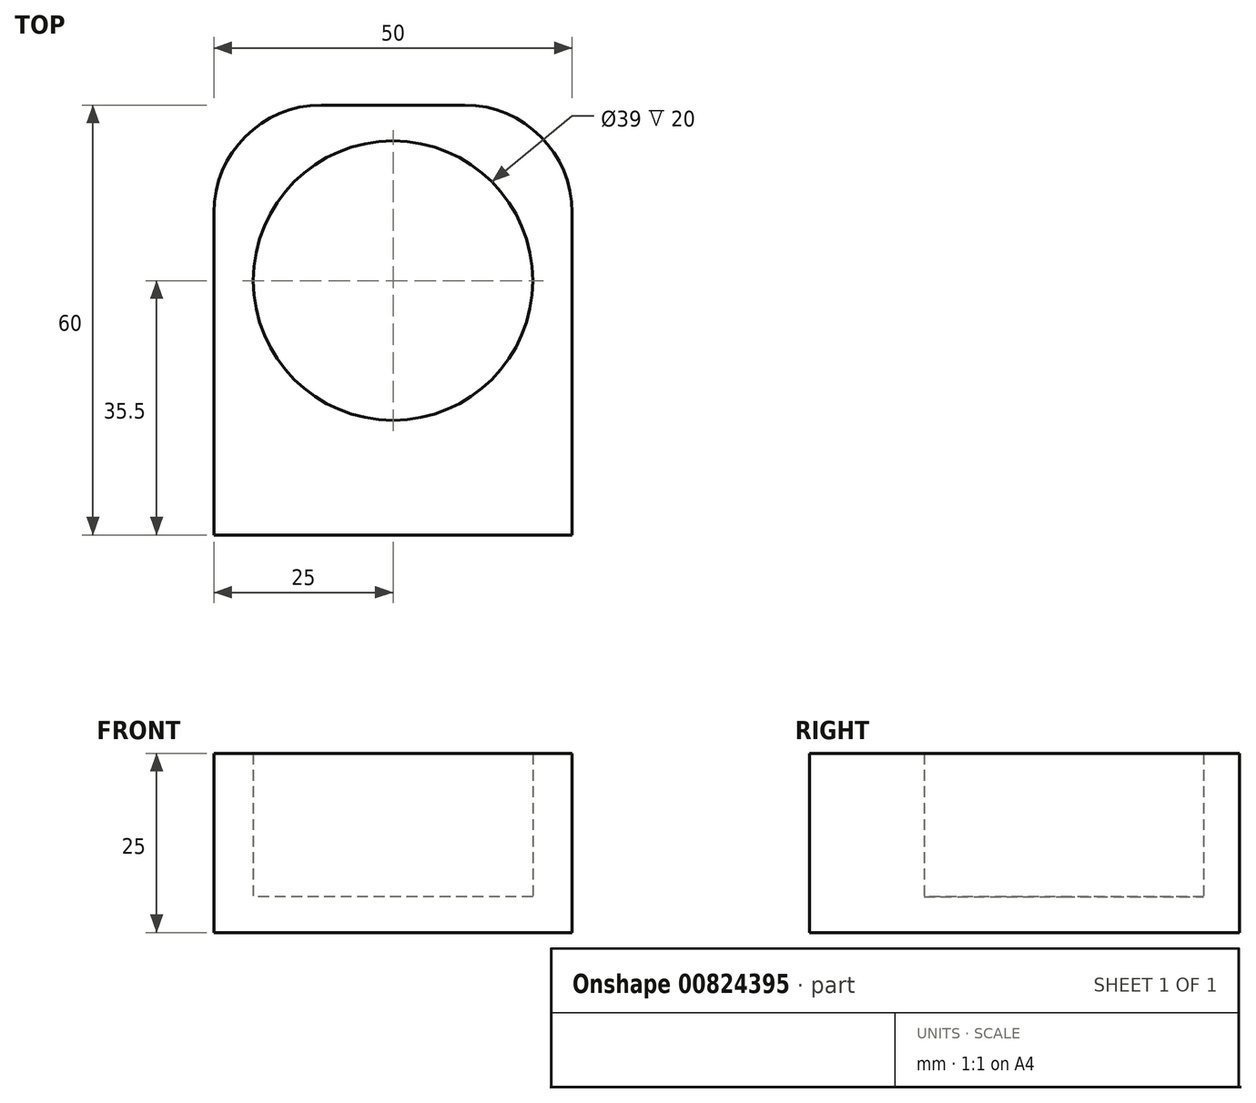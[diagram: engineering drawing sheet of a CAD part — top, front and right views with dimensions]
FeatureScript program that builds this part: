
annotation { "Feature Type Name" : "Feature", "Feature Type Description" : "" }
export const myFeature = defineFeature(function(context is Context, id is Id, definition is map)
    precondition{}
    {
        {
            var Q0;
            Q0=qCreatedBy(makeId("Top.planeOp"),FACE);
            var sketch = newSketch(context, id + "F0", { "sketchPlane" : qUnion([Q0])});
            skLineSegment(sketch, "E0.bottom", {"start": v(25, -30) * mm, "end": v(-25, -30) * mm});
            skLineSegment(sketch, "E0.top", {"start": v(25, 30) * mm, "end": v(-25, 30) * mm});
            skLineSegment(sketch, "E0.left", {"start": v(25, -30) * mm, "end": v(25, 30) * mm});
            skLineSegment(sketch, "E0.right", {"start": v(-25, -30) * mm, "end": v(-25, 30) * mm});
            skPoint(sketch, "E0.middle", {"position": v(0, 0) * mm});
            skPoint(sketch, "E1", {"position": v(0, 5.5) * mm});
            skCircle(sketch, "E2", {"center": v(0, 5.5) * mm, "radius": 19.5 * mm});
            skSolve(sketch);
        }
        {
            var Q0;
            Q0=makeQuery(id+"F0.imprint","IMPRINT",FACE,{"disambiguationData":[TD([[makeQuery(id+"F0.imprint","IMPRINT",EDGE,{"derivedFrom":sQuery(id+"F0.wireOp",EDGE,"E0.bottom")}),-1.0]])]});
            extrude(context, id + "F1", {"entities" : qUnion([Q0]), "depth" : 25 * mm, "offsetDistance" : 25 * mm});
        }
        {
            var Q0;
            Q0=makeQuery(id+"F1.opExtrude","SWEPT_EDGE",EDGE,{"disambiguationData":[OSD([sQuery(id+"F0.wireOp",EDGE,"E0.top"),sQuery(id+"F0.wireOp",EDGE,"E0.right")])]});
            fillet(context, id + "F2", {"entities" : qUnion([Q0]), "radius" : 15 * mm, "tangentPropagation" : true, "allowEdgeOverflow" : false});
        }
        {
            var Q0;
            Q0=makeQuery(id+"F1.opExtrude","SWEPT_EDGE",EDGE,{"disambiguationData":[OSD([sQuery(id+"F0.wireOp",EDGE,"E0.top"),sQuery(id+"F0.wireOp",EDGE,"E0.right")])]});
            var Q1;
            Q1=makeQuery(id+"F1.opExtrude","SWEPT_EDGE",EDGE,{"disambiguationData":[OSD([sQuery(id+"F0.wireOp",EDGE,"E0.top"),sQuery(id+"F0.wireOp",EDGE,"E0.left")])]});
            fillet(context, id + "F3", {"entities" : qUnion([Q0, Q1]), "radius" : 15 * mm, "tangentPropagation" : true, "allowEdgeOverflow" : false});
        }
        {
            var Q0;
            Q0=makeQuery(id+"F1.opExtrude","CAP_FACE",FACE,{"disambiguationData":[OSD([sQuery(id+"F0.wireOp",EDGE,"E0.bottom"),sQuery(id+"F0.wireOp",EDGE,"E0.top"),sQuery(id+"F0.wireOp",EDGE,"E0.left"),sQuery(id+"F0.wireOp",EDGE,"E0.right"),sQuery(id+"F0.wireOp",EDGE,"E2")])],"isStart":true});
            var sketch = newSketch(context, id + "F4", { "sketchPlane" : qUnion([Q0])});
            skPoint(sketch, "E3", {"position": v(0, -5.5) * mm});
            skCircle(sketch, "E4", {"center": v(0, -5.5) * mm, "radius": 19.5 * mm});
            skSolve(sketch);
        }
        {
            var Q0;
            Q0 = qSketchRegion(id + "F4", true);
            extrude(context, id + "F5", {"entities" : qUnion([Q0]), "operationType" : NewBodyOperationType.ADD, "oppositeDirection" : true, "depth" : 5 * mm, "offsetDistance" : 25 * mm});
        }
    });
